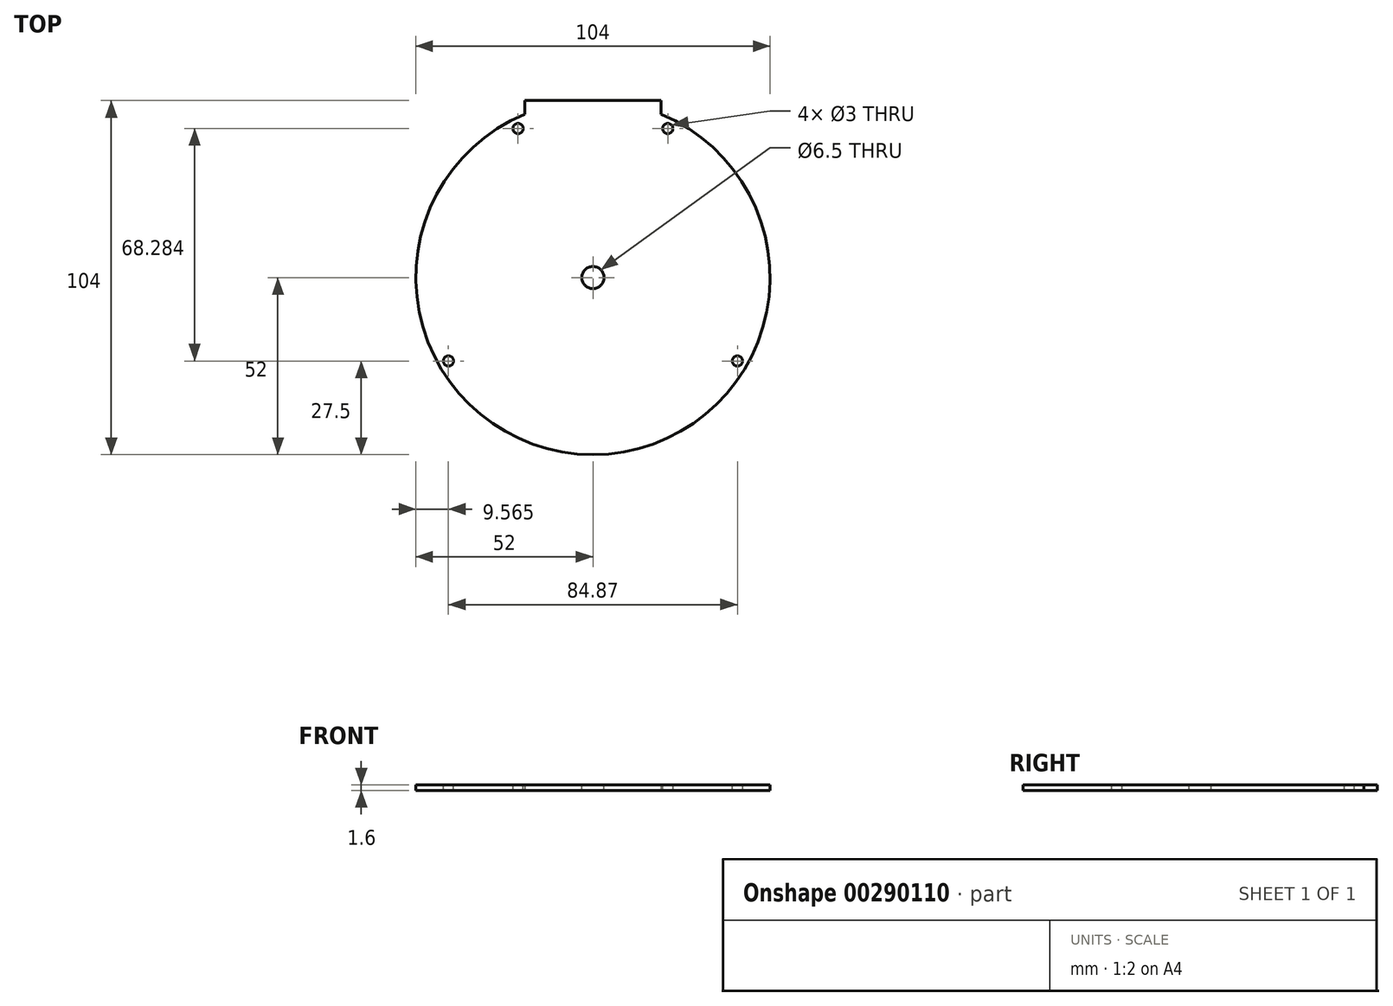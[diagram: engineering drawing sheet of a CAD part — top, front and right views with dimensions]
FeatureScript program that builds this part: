
annotation { "Feature Type Name" : "Feature", "Feature Type Description" : "" }
export const myFeature = defineFeature(function(context is Context, id is Id, definition is map)
    precondition{}
    {
        {
            var Q0;
            Q0=qCreatedBy(makeId("Top.planeOp"),FACE);
            var sketch = newSketch(context, id + "F0", { "sketchPlane" : qUnion([Q0])});
            skArc(sketch, "E0", {"start": v(-20, 48) * mm, "mid": v(0, -52) * mm, "end": v(20, 48) * mm});
            skLineSegment(sketch, "E1", {"start": v(-20, 48) * mm, "end": v(-20, 52) * mm});
            skLineSegment(sketch, "E2", {"start": v(-20, 52) * mm, "end": v(20, 52) * mm});
            skLineSegment(sketch, "E3", {"start": v(20, 52) * mm, "end": v(20, 48) * mm});
            skSolve(sketch);
        }
        {
            var Q0;
            Q0=makeQuery(id+"F0.imprint","IMPRINT",FACE,{"disambiguationData":[TD([[makeQuery(id+"F0.imprint","IMPRINT",EDGE,{"derivedFrom":sQuery(id+"F0.wireOp",EDGE,"E0")}),1.0]])]});
            extrude(context, id + "F1", {"entities" : qUnion([Q0]), "depth" : 1.6 * mm});
        }
        {
            var Q0;
            Q0=makeQuery(id+"F1.opExtrude","CAP_FACE",FACE,{"disambiguationData":[OSD([sQuery(id+"F0.wireOp",EDGE,"E0"),sQuery(id+"F0.wireOp",EDGE,"E1"),sQuery(id+"F0.wireOp",EDGE,"E2"),sQuery(id+"F0.wireOp",EDGE,"E3")])],"isStart":false});
            var sketch = newSketch(context, id + "F2", { "sketchPlane" : qUnion([Q0])});
            skCircle(sketch, "E4", {"center": v(-22, 43.78) * mm, "radius": 1.5 * mm});
            skCircle(sketch, "E5", {"center": v(22, 43.78) * mm, "radius": 1.56 * mm});
            skLineSegment(sketch, "E6", {"start": v(0, 0) * mm, "end": v(0, 57.68) * mm});
            skPoint(sketch, "E6.endSnap0", {"position": v(0, 52) * mm});
            skCircle(sketch, "E7", {"center": v(42.44, -24.5) * mm, "radius": 1.5 * mm});
            skCircle(sketch, "E8", {"center": v(-42.44, -24.5) * mm, "radius": 1.5 * mm});
            skSolve(sketch);
        }
        {
            var Q0;
            Q0=sQuery(id+"F2.wireOp",VERTEX,"E4.center");
            var Q1;
            Q1=sQuery(id+"F2.wireOp",VERTEX,"E5.center");
            var Q2;
            Q2=sQuery(id+"F2.wireOp",VERTEX,"E7.center");
            var Q3;
            Q3=sQuery(id+"F2.wireOp",VERTEX,"E8.center");
            var Q4;
            Q4=makeQuery(id+"F1.opExtrude","SWEPT_BODY",BODY,{"disambiguationData":[OSD([sQuery(id+"F0.wireOp",EDGE,"E0"),sQuery(id+"F0.wireOp",EDGE,"E1"),sQuery(id+"F0.wireOp",EDGE,"E2"),sQuery(id+"F0.wireOp",EDGE,"E3")])]});
            hole(context, id + "F3", {"style" : HoleStyle.SIMPLE, "endStyle" : HoleEndStyle.THROUGH, "holeDiameter" : 3 * mm, "tappedDepth" : 12 * mm, "tapClearance" : 3, "locations" : qUnion([Q0, Q1, Q2, Q3]), "scope" : qUnion([Q4])});
        }
        {
            var Q0;
            Q0=makeQuery(id+"F1.opExtrude","CAP_FACE",FACE,{"disambiguationData":[OSD([sQuery(id+"F0.wireOp",EDGE,"E0"),sQuery(id+"F0.wireOp",EDGE,"E1"),sQuery(id+"F0.wireOp",EDGE,"E2"),sQuery(id+"F0.wireOp",EDGE,"E3")])],"isStart":false});
            var sketch = newSketch(context, id + "F4", { "sketchPlane" : qUnion([Q0])});
            skCircle(sketch, "E9", {"center": v(0, 0) * mm, "radius": 3.25 * mm});
            skSolve(sketch);
        }
        {
            var Q0;
            Q0=sQuery(id+"F4.wireOp",VERTEX,"E9.center");
            var Q1;
            Q1=makeQuery(id+"F1.opExtrude","SWEPT_BODY",BODY,{"disambiguationData":[OSD([sQuery(id+"F0.wireOp",EDGE,"E0"),sQuery(id+"F0.wireOp",EDGE,"E1"),sQuery(id+"F0.wireOp",EDGE,"E2"),sQuery(id+"F0.wireOp",EDGE,"E3")])]});
            hole(context, id + "F5", {"style" : HoleStyle.SIMPLE, "endStyle" : HoleEndStyle.THROUGH, "holeDiameter" : 6.5 * mm, "tappedDepth" : 12 * mm, "tapClearance" : 3, "locations" : qUnion([Q0]), "scope" : qUnion([Q1])});
        }
    });
